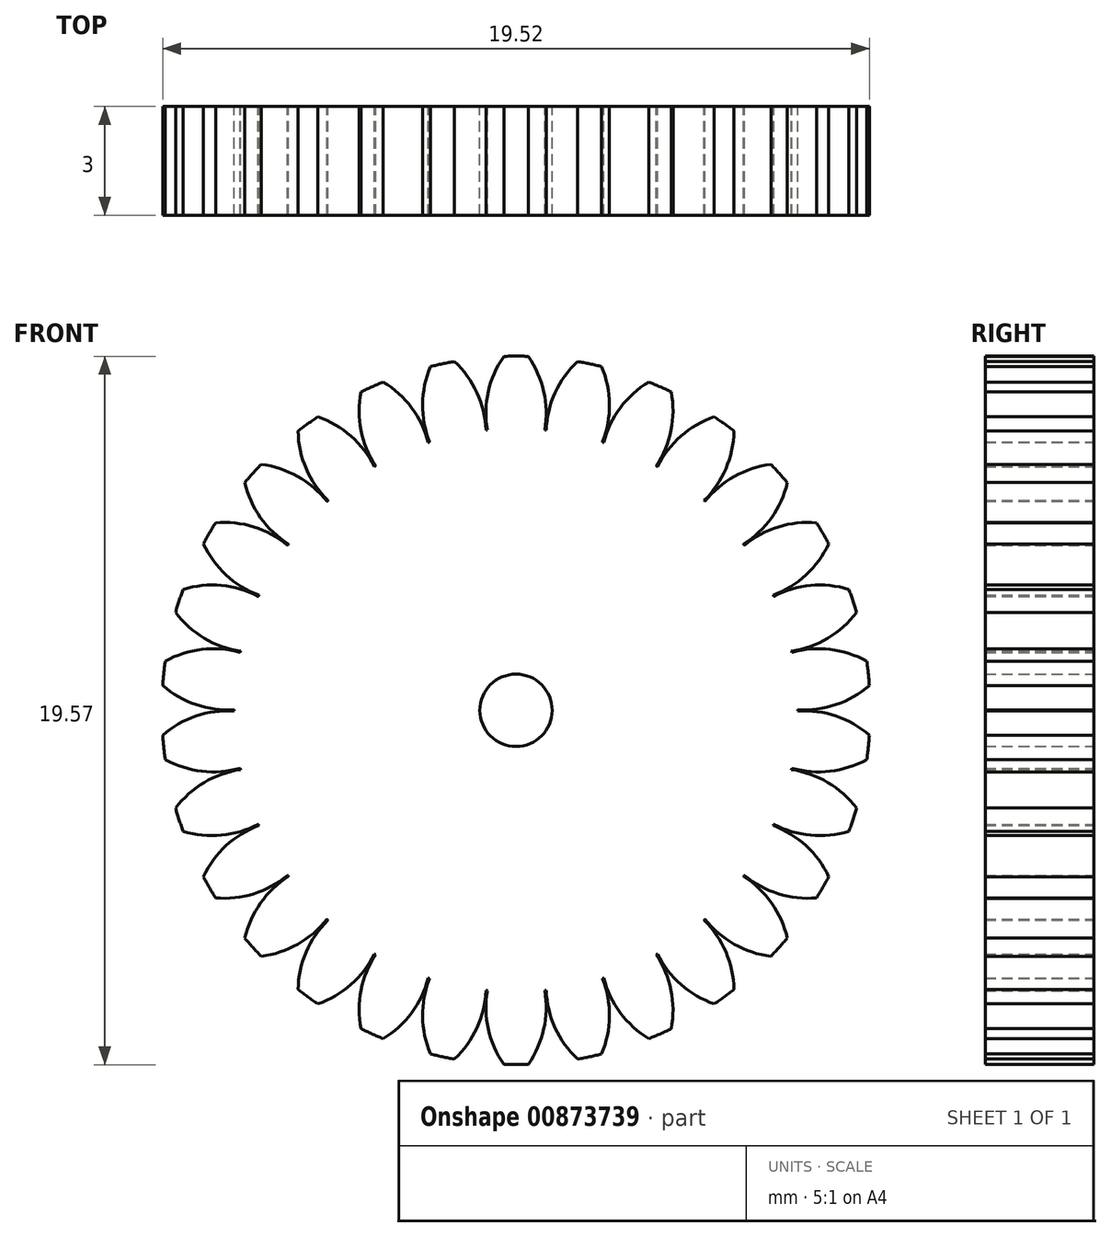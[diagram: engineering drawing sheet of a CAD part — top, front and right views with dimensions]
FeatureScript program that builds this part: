
annotation { "Feature Type Name" : "Feature", "Feature Type Description" : "" }
export const myFeature = defineFeature(function(context is Context, id is Id, definition is map)
    precondition{}
    {
        {
            var Q0;
            Q0=qCreatedBy(makeId("Front.planeOp"),FACE);
            var sketch = newSketch(context, id + "F0", { "sketchPlane" : qUnion([Q0])});
            skCircle(sketch, "E0", {"center": v(0, 0) * mm, "radius": 7.79 * mm});
            skArc(sketch, "E1", {"start": v(0.34, 9.78) * mm, "mid": v(0, 9.79) * mm, "end": v(-0.34, 9.78) * mm});
            skArc(sketch, "E2", {"start": v(-0.34, 9.78) * mm, "mid": v(-0.77, 8.8) * mm, "end": v(-0.8, 7.74) * mm});
            skArc(sketch, "E3.MirrorCS", {"start": v(0.34, 9.78) * mm, "mid": v(0.77, 8.8) * mm, "end": v(0.8, 7.74) * mm});
            skArc(sketch, "E4.1.0", {"start": v(-1.7, 9.64) * mm, "mid": v(-1.08, 8.77) * mm, "end": v(-0.83, 7.74) * mm});
            skArc(sketch, "E4.1.1", {"start": v(-1.7, 9.64) * mm, "mid": v(-2.03, 9.57) * mm, "end": v(-2.36, 9.5) * mm});
            skArc(sketch, "E4.1.2", {"start": v(-2.36, 9.5) * mm, "mid": v(-2.58, 8.45) * mm, "end": v(-2.39, 7.4) * mm});
            skArc(sketch, "E4.2.0", {"start": v(-3.67, 9.07) * mm, "mid": v(-2.88, 8.36) * mm, "end": v(-2.42, 7.4) * mm});
            skArc(sketch, "E4.2.1", {"start": v(-3.67, 9.07) * mm, "mid": v(-3.98, 8.94) * mm, "end": v(-4.29, 8.8) * mm});
            skArc(sketch, "E4.2.2", {"start": v(-4.29, 8.8) * mm, "mid": v(-4.28, 7.73) * mm, "end": v(-3.88, 6.75) * mm});
            skArc(sketch, "E4.3.0", {"start": v(-5.48, 8.1) * mm, "mid": v(-4.56, 7.58) * mm, "end": v(-3.9, 6.73) * mm});
            skArc(sketch, "E4.3.1", {"start": v(-5.48, 8.1) * mm, "mid": v(-5.75, 7.92) * mm, "end": v(-6.02, 7.71) * mm});
            skArc(sketch, "E4.3.2", {"start": v(-6.02, 7.71) * mm, "mid": v(-5.8, 6.67) * mm, "end": v(-5.2, 5.8) * mm});
            skArc(sketch, "E4.4.0", {"start": v(-7.04, 6.8) * mm, "mid": v(-6.03, 6.46) * mm, "end": v(-5.22, 5.77) * mm});
            skArc(sketch, "E4.4.1", {"start": v(-7.04, 6.8) * mm, "mid": v(-7.27, 6.55) * mm, "end": v(-7.5, 6.3) * mm});
            skArc(sketch, "E4.4.2", {"start": v(-7.5, 6.3) * mm, "mid": v(-7.06, 5.32) * mm, "end": v(-6.29, 4.6) * mm});
            skArc(sketch, "E4.5.0", {"start": v(-8.3, 5.18) * mm, "mid": v(-7.24, 5.07) * mm, "end": v(-6.3, 4.56) * mm});
            skArc(sketch, "E4.5.1", {"start": v(-8.3, 5.18) * mm, "mid": v(-8.47, 4.9) * mm, "end": v(-8.64, 4.6) * mm});
            skArc(sketch, "E4.5.2", {"start": v(-8.64, 4.6) * mm, "mid": v(-8.01, 3.74) * mm, "end": v(-7.1, 3.18) * mm});
            skArc(sketch, "E4.6.0", {"start": v(-9.2, 3.34) * mm, "mid": v(-8.14, 3.45) * mm, "end": v(-7.12, 3.15) * mm});
            skArc(sketch, "E4.6.1", {"start": v(-9.2, 3.34) * mm, "mid": v(-9.3, 3.02) * mm, "end": v(-9.4, 2.7) * mm});
            skArc(sketch, "E4.6.2", {"start": v(-9.4, 2.7) * mm, "mid": v(-8.61, 2) * mm, "end": v(-7.61, 1.64) * mm});
            skArc(sketch, "E4.7.0", {"start": v(-9.7, 1.36) * mm, "mid": v(-8.68, 1.68) * mm, "end": v(-7.62, 1.6) * mm});
            skArc(sketch, "E4.7.1", {"start": v(-9.7, 1.36) * mm, "mid": v(-9.73, 1.02) * mm, "end": v(-9.76, 0.69) * mm});
            skArc(sketch, "E4.7.2", {"start": v(-9.76, 0.69) * mm, "mid": v(-8.84, 0.16) * mm, "end": v(-7.78, 0.02) * mm});
            skArc(sketch, "E4.8.0", {"start": v(-9.76, -0.69) * mm, "mid": v(-8.84, -0.16) * mm, "end": v(-7.78, -0.02) * mm});
            skArc(sketch, "E4.8.1", {"start": v(-9.76, -0.69) * mm, "mid": v(-9.73, -1.02) * mm, "end": v(-9.7, -1.36) * mm});
            skArc(sketch, "E4.8.2", {"start": v(-9.7, -1.36) * mm, "mid": v(-8.68, -1.68) * mm, "end": v(-7.62, -1.6) * mm});
            skArc(sketch, "E5.1.9.0", {"start": v(-9.4, -2.7) * mm, "mid": v(-8.61, -2) * mm, "end": v(-7.61, -1.64) * mm});
            skArc(sketch, "E5.4.9.0", {"start": v(-9.4, -2.7) * mm, "mid": v(-9.3, -3.02) * mm, "end": v(-9.2, -3.34) * mm});
            skArc(sketch, "E5.8.9.0", {"start": v(-9.2, -3.34) * mm, "mid": v(-8.14, -3.45) * mm, "end": v(-7.12, -3.15) * mm});
            skArc(sketch, "E5.1.10.0", {"start": v(-8.64, -4.6) * mm, "mid": v(-8.01, -3.74) * mm, "end": v(-7.1, -3.18) * mm});
            skArc(sketch, "E5.4.10.0", {"start": v(-8.64, -4.6) * mm, "mid": v(-8.47, -4.9) * mm, "end": v(-8.3, -5.18) * mm});
            skArc(sketch, "E5.8.10.0", {"start": v(-8.3, -5.18) * mm, "mid": v(-7.24, -5.07) * mm, "end": v(-6.3, -4.56) * mm});
            skArc(sketch, "E5.1.11.0", {"start": v(-7.5, -6.3) * mm, "mid": v(-7.06, -5.32) * mm, "end": v(-6.29, -4.6) * mm});
            skArc(sketch, "E5.4.11.0", {"start": v(-7.5, -6.3) * mm, "mid": v(-7.27, -6.55) * mm, "end": v(-7.04, -6.8) * mm});
            skArc(sketch, "E5.8.11.0", {"start": v(-7.04, -6.8) * mm, "mid": v(-6.03, -6.46) * mm, "end": v(-5.22, -5.77) * mm});
            skArc(sketch, "E5.1.12.0", {"start": v(-6.02, -7.71) * mm, "mid": v(-5.8, -6.67) * mm, "end": v(-5.2, -5.8) * mm});
            skArc(sketch, "E5.4.12.0", {"start": v(-6.02, -7.71) * mm, "mid": v(-5.75, -7.92) * mm, "end": v(-5.48, -8.1) * mm});
            skArc(sketch, "E5.8.12.0", {"start": v(-5.48, -8.1) * mm, "mid": v(-4.56, -7.58) * mm, "end": v(-3.9, -6.73) * mm});
            skArc(sketch, "E5.1.13.0", {"start": v(-4.29, -8.8) * mm, "mid": v(-4.28, -7.73) * mm, "end": v(-3.88, -6.75) * mm});
            skArc(sketch, "E5.4.13.0", {"start": v(-4.29, -8.8) * mm, "mid": v(-3.98, -8.94) * mm, "end": v(-3.67, -9.07) * mm});
            skArc(sketch, "E5.8.13.0", {"start": v(-3.67, -9.07) * mm, "mid": v(-2.88, -8.36) * mm, "end": v(-2.42, -7.4) * mm});
            skArc(sketch, "E5.1.14.0", {"start": v(-2.36, -9.5) * mm, "mid": v(-2.58, -8.45) * mm, "end": v(-2.39, -7.4) * mm});
            skArc(sketch, "E5.4.14.0", {"start": v(-2.36, -9.5) * mm, "mid": v(-2.03, -9.57) * mm, "end": v(-1.7, -9.64) * mm});
            skArc(sketch, "E5.8.14.0", {"start": v(-1.7, -9.64) * mm, "mid": v(-1.08, -8.77) * mm, "end": v(-0.83, -7.74) * mm});
            skArc(sketch, "E5.1.15.0", {"start": v(-0.34, -9.78) * mm, "mid": v(-0.77, -8.8) * mm, "end": v(-0.8, -7.74) * mm});
            skArc(sketch, "E5.4.15.0", {"start": v(-0.34, -9.78) * mm, "mid": v(0, -9.79) * mm, "end": v(0.34, -9.78) * mm});
            skArc(sketch, "E5.8.15.0", {"start": v(0.34, -9.78) * mm, "mid": v(0.77, -8.8) * mm, "end": v(0.8, -7.74) * mm});
            skArc(sketch, "E5.1.16.0", {"start": v(1.7, -9.64) * mm, "mid": v(1.08, -8.77) * mm, "end": v(0.83, -7.74) * mm});
            skArc(sketch, "E5.4.16.0", {"start": v(1.7, -9.64) * mm, "mid": v(2.03, -9.57) * mm, "end": v(2.36, -9.5) * mm});
            skArc(sketch, "E5.8.16.0", {"start": v(2.36, -9.5) * mm, "mid": v(2.58, -8.45) * mm, "end": v(2.39, -7.4) * mm});
            skArc(sketch, "E5.1.17.0", {"start": v(3.67, -9.07) * mm, "mid": v(2.88, -8.36) * mm, "end": v(2.42, -7.4) * mm});
            skArc(sketch, "E5.4.17.0", {"start": v(3.67, -9.07) * mm, "mid": v(3.98, -8.94) * mm, "end": v(4.29, -8.8) * mm});
            skArc(sketch, "E5.8.17.0", {"start": v(4.29, -8.8) * mm, "mid": v(4.28, -7.73) * mm, "end": v(3.88, -6.75) * mm});
            skArc(sketch, "E6.1.18.0", {"start": v(5.48, -8.1) * mm, "mid": v(4.56, -7.58) * mm, "end": v(3.9, -6.73) * mm});
            skArc(sketch, "E6.4.18.0", {"start": v(5.48, -8.1) * mm, "mid": v(5.75, -7.92) * mm, "end": v(6.02, -7.71) * mm});
            skArc(sketch, "E6.8.18.0", {"start": v(6.02, -7.71) * mm, "mid": v(5.8, -6.67) * mm, "end": v(5.2, -5.8) * mm});
            skArc(sketch, "E7.1.19.0", {"start": v(7.04, -6.8) * mm, "mid": v(6.03, -6.46) * mm, "end": v(5.22, -5.77) * mm});
            skArc(sketch, "E7.4.19.0", {"start": v(7.04, -6.8) * mm, "mid": v(7.27, -6.55) * mm, "end": v(7.5, -6.3) * mm});
            skArc(sketch, "E7.8.19.0", {"start": v(7.5, -6.3) * mm, "mid": v(7.06, -5.32) * mm, "end": v(6.29, -4.6) * mm});
            skArc(sketch, "E8.1.20.0", {"start": v(8.3, -5.18) * mm, "mid": v(7.24, -5.07) * mm, "end": v(6.3, -4.56) * mm});
            skArc(sketch, "E8.4.20.0", {"start": v(8.3, -5.18) * mm, "mid": v(8.47, -4.9) * mm, "end": v(8.64, -4.6) * mm});
            skArc(sketch, "E8.8.20.0", {"start": v(8.64, -4.6) * mm, "mid": v(8.01, -3.74) * mm, "end": v(7.1, -3.18) * mm});
            skArc(sketch, "E8.1.21.0", {"start": v(9.2, -3.34) * mm, "mid": v(8.14, -3.45) * mm, "end": v(7.12, -3.15) * mm});
            skArc(sketch, "E8.4.21.0", {"start": v(9.2, -3.34) * mm, "mid": v(9.3, -3.02) * mm, "end": v(9.4, -2.7) * mm});
            skArc(sketch, "E8.8.21.0", {"start": v(9.4, -2.7) * mm, "mid": v(8.61, -2) * mm, "end": v(7.61, -1.64) * mm});
            skArc(sketch, "E8.1.22.0", {"start": v(9.7, -1.36) * mm, "mid": v(8.68, -1.68) * mm, "end": v(7.62, -1.6) * mm});
            skArc(sketch, "E8.4.22.0", {"start": v(9.7, -1.36) * mm, "mid": v(9.73, -1.02) * mm, "end": v(9.76, -0.69) * mm});
            skArc(sketch, "E8.8.22.0", {"start": v(9.76, -0.69) * mm, "mid": v(8.84, -0.16) * mm, "end": v(7.78, -0.02) * mm});
            skArc(sketch, "E8.1.23.0", {"start": v(9.76, 0.69) * mm, "mid": v(8.84, 0.16) * mm, "end": v(7.78, 0.02) * mm});
            skArc(sketch, "E8.4.23.0", {"start": v(9.76, 0.69) * mm, "mid": v(9.73, 1.02) * mm, "end": v(9.7, 1.36) * mm});
            skArc(sketch, "E8.8.23.0", {"start": v(9.7, 1.36) * mm, "mid": v(8.68, 1.68) * mm, "end": v(7.62, 1.6) * mm});
            skArc(sketch, "E8.1.24.0", {"start": v(9.4, 2.7) * mm, "mid": v(8.61, 2) * mm, "end": v(7.61, 1.64) * mm});
            skArc(sketch, "E8.4.24.0", {"start": v(9.4, 2.7) * mm, "mid": v(9.3, 3.02) * mm, "end": v(9.2, 3.34) * mm});
            skArc(sketch, "E8.8.24.0", {"start": v(9.2, 3.34) * mm, "mid": v(8.14, 3.45) * mm, "end": v(7.12, 3.15) * mm});
            skArc(sketch, "E8.1.25.0", {"start": v(8.64, 4.6) * mm, "mid": v(8.01, 3.74) * mm, "end": v(7.1, 3.18) * mm});
            skArc(sketch, "E8.4.25.0", {"start": v(8.64, 4.6) * mm, "mid": v(8.47, 4.9) * mm, "end": v(8.3, 5.18) * mm});
            skArc(sketch, "E8.8.25.0", {"start": v(8.3, 5.18) * mm, "mid": v(7.24, 5.07) * mm, "end": v(6.3, 4.56) * mm});
            skArc(sketch, "E8.1.26.0", {"start": v(7.5, 6.3) * mm, "mid": v(7.06, 5.32) * mm, "end": v(6.29, 4.6) * mm});
            skArc(sketch, "E8.4.26.0", {"start": v(7.5, 6.3) * mm, "mid": v(7.27, 6.55) * mm, "end": v(7.04, 6.8) * mm});
            skArc(sketch, "E8.8.26.0", {"start": v(7.04, 6.8) * mm, "mid": v(6.03, 6.46) * mm, "end": v(5.22, 5.77) * mm});
            skArc(sketch, "E8.1.27.0", {"start": v(6.02, 7.71) * mm, "mid": v(5.8, 6.67) * mm, "end": v(5.2, 5.8) * mm});
            skArc(sketch, "E8.4.27.0", {"start": v(6.02, 7.71) * mm, "mid": v(5.75, 7.92) * mm, "end": v(5.48, 8.1) * mm});
            skArc(sketch, "E8.8.27.0", {"start": v(5.48, 8.1) * mm, "mid": v(4.56, 7.58) * mm, "end": v(3.9, 6.73) * mm});
            skArc(sketch, "E8.1.28.0", {"start": v(4.29, 8.8) * mm, "mid": v(4.28, 7.73) * mm, "end": v(3.88, 6.75) * mm});
            skArc(sketch, "E8.4.28.0", {"start": v(4.29, 8.8) * mm, "mid": v(3.98, 8.94) * mm, "end": v(3.67, 9.07) * mm});
            skArc(sketch, "E8.8.28.0", {"start": v(3.67, 9.07) * mm, "mid": v(2.88, 8.36) * mm, "end": v(2.42, 7.4) * mm});
            skArc(sketch, "E8.1.29.0", {"start": v(2.36, 9.5) * mm, "mid": v(2.58, 8.45) * mm, "end": v(2.39, 7.4) * mm});
            skArc(sketch, "E8.4.29.0", {"start": v(2.36, 9.5) * mm, "mid": v(2.03, 9.57) * mm, "end": v(1.7, 9.64) * mm});
            skArc(sketch, "E8.8.29.0", {"start": v(1.7, 9.64) * mm, "mid": v(1.08, 8.77) * mm, "end": v(0.83, 7.74) * mm});
            skSolve(sketch);
        }
        {
            var Q0;
            Q0=qSketchRegion(id+"F0",true);
            extrude(context, id + "F1", {"entities" : qUnion([Q0]), "depth" : 3 * mm, "offsetDistance" : 25 * mm});
        }
        {
            var Q0;
            Q0=makeQuery(id+"F1.opExtrude","CAP_FACE",FACE,{"disambiguationData":[OSD([sQuery(id+"F0.wireOp",EDGE,"E0"),sQuery(id+"F0.wireOp",EDGE,"E1"),sQuery(id+"F0.wireOp",EDGE,"E2"),sQuery(id+"F0.wireOp",EDGE,"E3.MirrorCS"),sQuery(id+"F0.wireOp",EDGE,"E4.1.0"),sQuery(id+"F0.wireOp",EDGE,"E4.1.1"),sQuery(id+"F0.wireOp",EDGE,"E4.1.2"),sQuery(id+"F0.wireOp",EDGE,"E4.2.0"),sQuery(id+"F0.wireOp",EDGE,"E4.2.1"),sQuery(id+"F0.wireOp",EDGE,"E4.2.2"),sQuery(id+"F0.wireOp",EDGE,"E4.3.0"),sQuery(id+"F0.wireOp",EDGE,"E4.3.1"),sQuery(id+"F0.wireOp",EDGE,"E4.3.2"),sQuery(id+"F0.wireOp",EDGE,"E4.4.0"),sQuery(id+"F0.wireOp",EDGE,"E4.4.1"),sQuery(id+"F0.wireOp",EDGE,"E4.4.2"),sQuery(id+"F0.wireOp",EDGE,"E4.5.0"),sQuery(id+"F0.wireOp",EDGE,"E4.5.1"),sQuery(id+"F0.wireOp",EDGE,"E4.5.2"),sQuery(id+"F0.wireOp",EDGE,"E4.6.0"),sQuery(id+"F0.wireOp",EDGE,"E4.6.1"),sQuery(id+"F0.wireOp",EDGE,"E4.6.2"),sQuery(id+"F0.wireOp",EDGE,"E4.7.0"),sQuery(id+"F0.wireOp",EDGE,"E4.7.1"),sQuery(id+"F0.wireOp",EDGE,"E4.7.2"),sQuery(id+"F0.wireOp",EDGE,"E4.8.0"),sQuery(id+"F0.wireOp",EDGE,"E4.8.1"),sQuery(id+"F0.wireOp",EDGE,"E4.8.2")])],"isStart":true});
            var sketch = newSketch(context, id + "F2", { "sketchPlane" : qUnion([Q0])});
            skCircle(sketch, "E9", {"center": v(0, 0) * mm, "radius": 1 * mm});
            skSolve(sketch);
        }
        {
            var Q0;
            Q0=makeQuery(id+"F2.imprint","IMPRINT",FACE,{"disambiguationData":[TD([[makeQuery(id+"F2.imprint","IMPRINT",EDGE,{"derivedFrom":sQuery(id+"F2.wireOp",EDGE,"E9")}),1.0]])]});
            extrude(context, id + "F3", {"entities" : qUnion([Q0]), "operationType" : NewBodyOperationType.REMOVE, "endBound" : BoundingType.THROUGH_ALL, "oppositeDirection" : true, "depth" : 25 * mm, "offsetDistance" : 25 * mm});
        }
        {
            var Q0;
            Q0=makeQuery(id+"F1.opExtrude","SWEPT_BODY",BODY,{"disambiguationData":[OSD([sQuery(id+"F0.wireOp",EDGE,"E0"),sQuery(id+"F0.wireOp",EDGE,"E1"),sQuery(id+"F0.wireOp",EDGE,"E2"),sQuery(id+"F0.wireOp",EDGE,"E3.MirrorCS"),sQuery(id+"F0.wireOp",EDGE,"E4.1.0"),sQuery(id+"F0.wireOp",EDGE,"E4.1.1"),sQuery(id+"F0.wireOp",EDGE,"E4.1.2"),sQuery(id+"F0.wireOp",EDGE,"E4.2.0"),sQuery(id+"F0.wireOp",EDGE,"E4.2.1"),sQuery(id+"F0.wireOp",EDGE,"E4.2.2"),sQuery(id+"F0.wireOp",EDGE,"E4.3.0"),sQuery(id+"F0.wireOp",EDGE,"E4.3.1"),sQuery(id+"F0.wireOp",EDGE,"E4.3.2"),sQuery(id+"F0.wireOp",EDGE,"E4.4.0"),sQuery(id+"F0.wireOp",EDGE,"E4.4.1"),sQuery(id+"F0.wireOp",EDGE,"E4.4.2"),sQuery(id+"F0.wireOp",EDGE,"E4.5.0"),sQuery(id+"F0.wireOp",EDGE,"E4.5.1"),sQuery(id+"F0.wireOp",EDGE,"E4.5.2"),sQuery(id+"F0.wireOp",EDGE,"E4.6.0"),sQuery(id+"F0.wireOp",EDGE,"E4.6.1"),sQuery(id+"F0.wireOp",EDGE,"E4.6.2"),sQuery(id+"F0.wireOp",EDGE,"E4.7.0"),sQuery(id+"F0.wireOp",EDGE,"E4.7.1"),sQuery(id+"F0.wireOp",EDGE,"E4.7.2"),sQuery(id+"F0.wireOp",EDGE,"E4.8.0"),sQuery(id+"F0.wireOp",EDGE,"E4.8.1"),sQuery(id+"F0.wireOp",EDGE,"E4.8.2")])]});
            transform(context, id + "F4", {"entities" : qUnion([Q0]), "transformType" : TransformType.TRANSLATION_3D, "dx" : 0 * mm, "dy" : 0 * mm, "dz" : 0 * mm, "makeCopy" : true});
        }
        {
            var Q0;
            Q0=makeQuery(id+"F4.opPattern","COPY",BODY,{"derivedFrom":makeQuery(id+"F1.opExtrude","SWEPT_BODY",BODY,{"disambiguationData":[OSD([sQuery(id+"F0.wireOp",EDGE,"E0"),sQuery(id+"F0.wireOp",EDGE,"E1"),sQuery(id+"F0.wireOp",EDGE,"E2"),sQuery(id+"F0.wireOp",EDGE,"E3.MirrorCS"),sQuery(id+"F0.wireOp",EDGE,"E4.1.0"),sQuery(id+"F0.wireOp",EDGE,"E4.1.1"),sQuery(id+"F0.wireOp",EDGE,"E4.1.2"),sQuery(id+"F0.wireOp",EDGE,"E4.2.0"),sQuery(id+"F0.wireOp",EDGE,"E4.2.1"),sQuery(id+"F0.wireOp",EDGE,"E4.2.2"),sQuery(id+"F0.wireOp",EDGE,"E4.3.0"),sQuery(id+"F0.wireOp",EDGE,"E4.3.1"),sQuery(id+"F0.wireOp",EDGE,"E4.3.2"),sQuery(id+"F0.wireOp",EDGE,"E4.4.0"),sQuery(id+"F0.wireOp",EDGE,"E4.4.1"),sQuery(id+"F0.wireOp",EDGE,"E4.4.2"),sQuery(id+"F0.wireOp",EDGE,"E4.5.0"),sQuery(id+"F0.wireOp",EDGE,"E4.5.1"),sQuery(id+"F0.wireOp",EDGE,"E4.5.2"),sQuery(id+"F0.wireOp",EDGE,"E4.6.0"),sQuery(id+"F0.wireOp",EDGE,"E4.6.1"),sQuery(id+"F0.wireOp",EDGE,"E4.6.2"),sQuery(id+"F0.wireOp",EDGE,"E4.7.0"),sQuery(id+"F0.wireOp",EDGE,"E4.7.1"),sQuery(id+"F0.wireOp",EDGE,"E4.7.2"),sQuery(id+"F0.wireOp",EDGE,"E4.8.0"),sQuery(id+"F0.wireOp",EDGE,"E4.8.1"),sQuery(id+"F0.wireOp",EDGE,"E4.8.2")])]}),"instanceName":"1"});
            deleteBodies(context, id + "F5", {"entities" : qUnion([Q0])});
        }
    });
